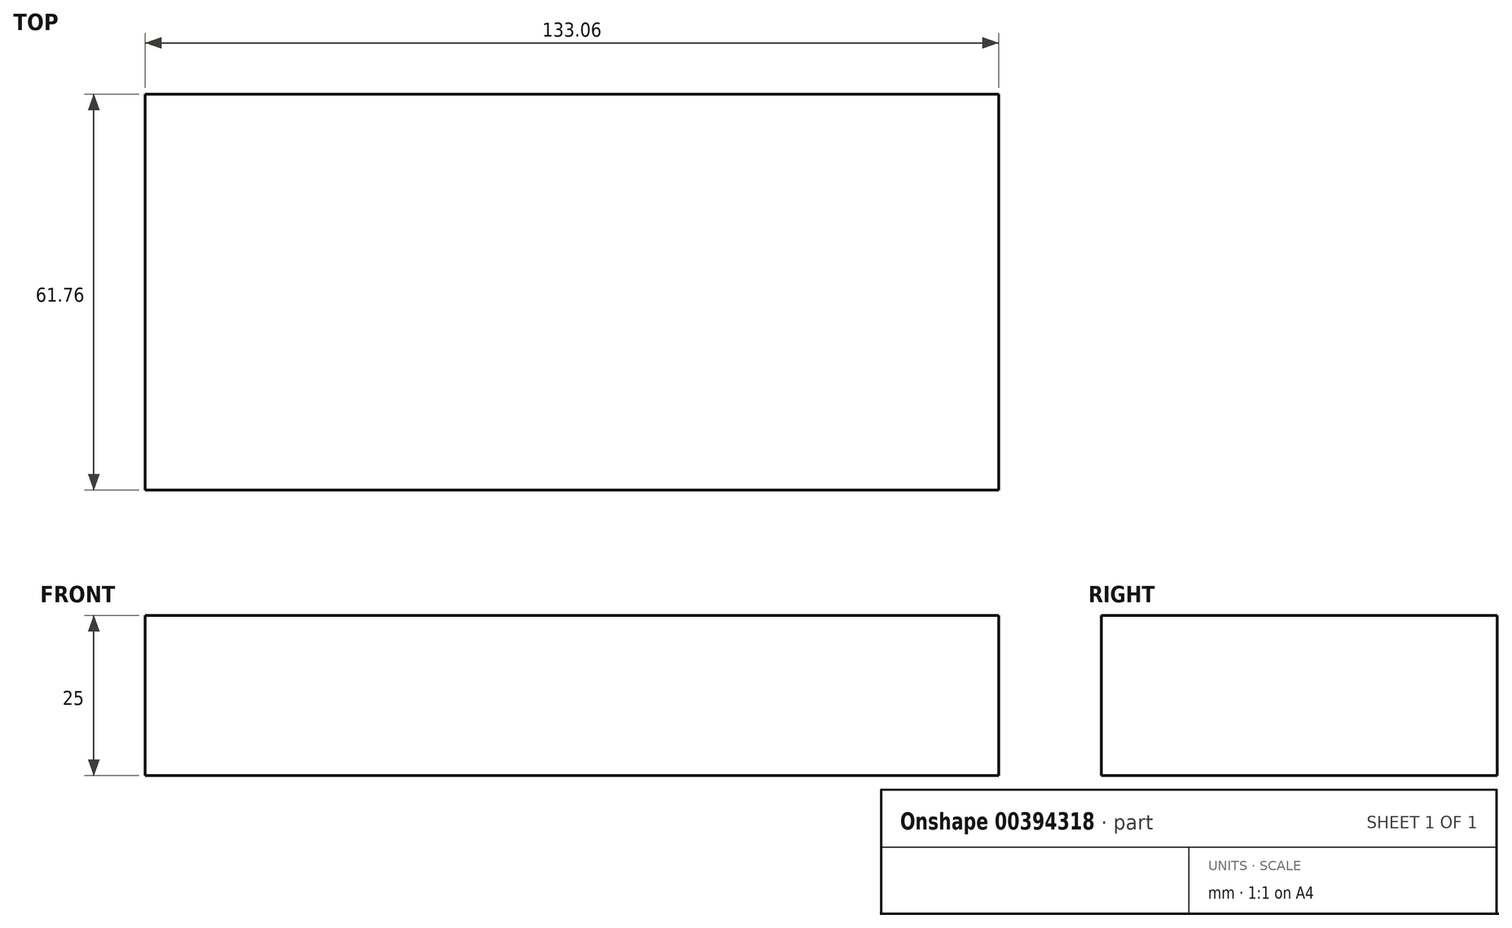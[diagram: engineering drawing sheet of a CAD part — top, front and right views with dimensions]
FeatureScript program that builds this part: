
annotation { "Feature Type Name" : "Feature", "Feature Type Description" : "" }
export const myFeature = defineFeature(function(context is Context, id is Id, definition is map)
    precondition{}
    {
        {
            var Q0;
            Q0=qCreatedBy(makeId("Top.planeOp"),FACE);
            var sketch = newSketch(context, id + "F0", { "sketchPlane" : qUnion([Q0])});
            skLineSegment(sketch, "E0.bottom", {"start": v(-73.56, 34.2) * mm, "end": v(59.5, 34.2) * mm});
            skLineSegment(sketch, "E0.top", {"start": v(-73.56, -27.56) * mm, "end": v(59.5, -27.56) * mm});
            skLineSegment(sketch, "E0.left", {"start": v(-73.56, 34.2) * mm, "end": v(-73.56, -27.56) * mm});
            skLineSegment(sketch, "E0.right", {"start": v(59.5, 34.2) * mm, "end": v(59.5, -27.56) * mm});
            skSolve(sketch);
        }
        {
            var Q0;
            Q0 = qSketchRegion(id + "F0", true);
            extrude(context, id + "F1", {"entities" : qUnion([Q0]), "depth" : 25 * mm});
        }
    });
